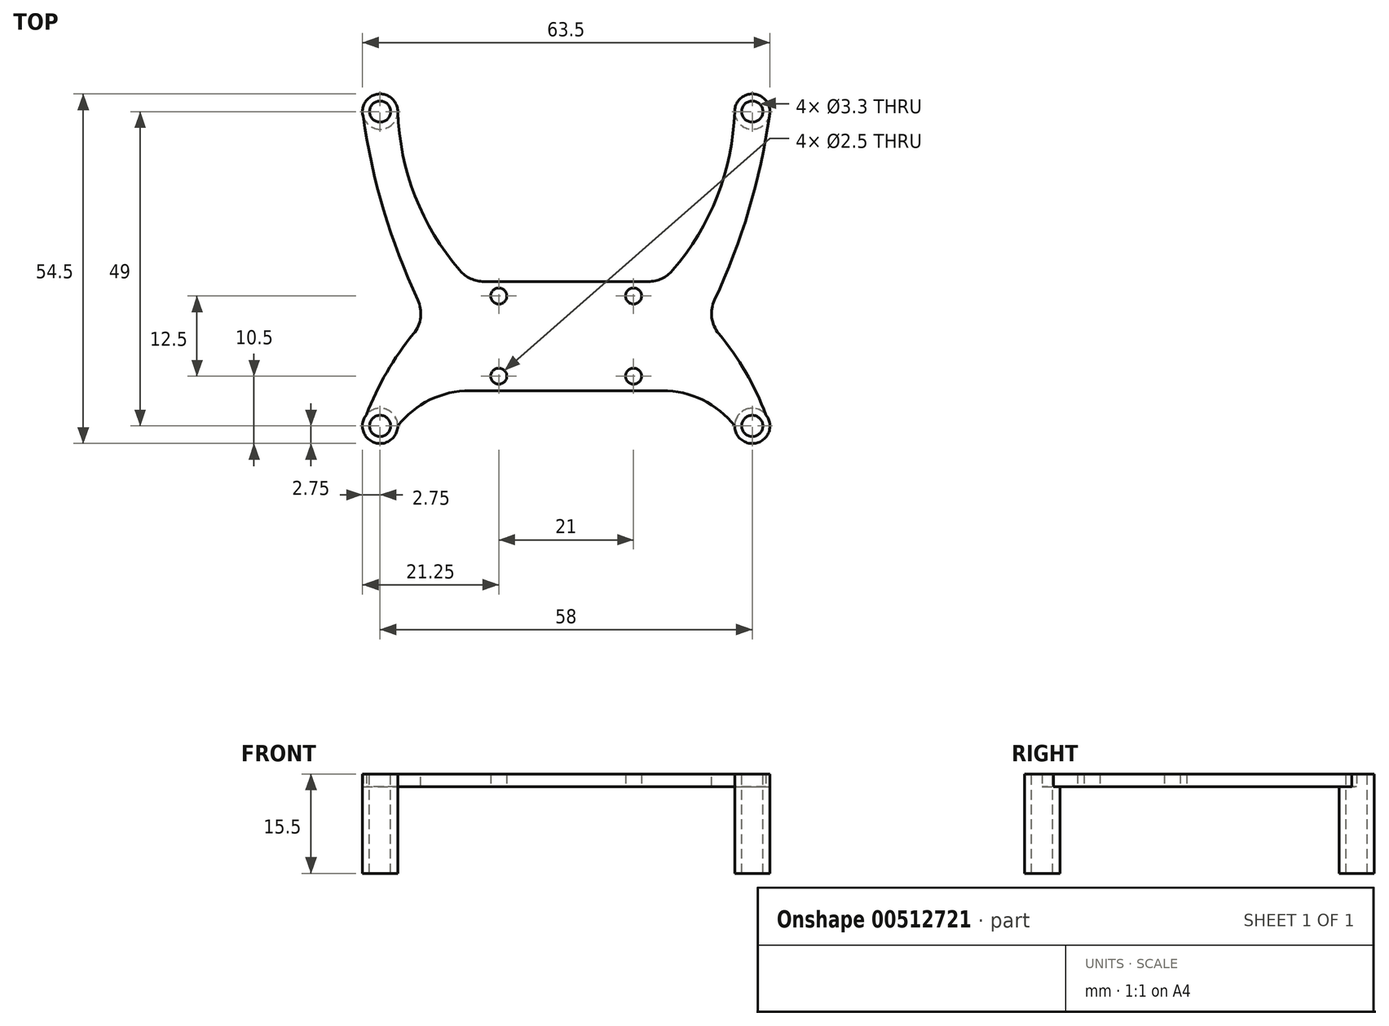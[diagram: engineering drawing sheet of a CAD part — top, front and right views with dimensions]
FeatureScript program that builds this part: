
annotation { "Feature Type Name" : "Feature", "Feature Type Description" : "" }
export const myFeature = defineFeature(function(context is Context, id is Id, definition is map)
    precondition{}
    {
        {
            var Q0;
            Q0=qCreatedBy(makeId("Top.planeOp"),FACE);
            var sketch = newSketch(context, id + "F0", { "sketchPlane" : qUnion([Q0])});
            skCircle(sketch, "E0", {"center": v(-29, 0) * mm, "radius": 2.75 * mm});
            skCircle(sketch, "E1", {"center": v(29, 0) * mm, "radius": 2.75 * mm});
            skLineSegment(sketch, "E2", {"start": v(-29, 0) * mm, "end": v(29, 0) * mm, "construction": true});
            skPoint(sketch, "E3", {"position": v(0, 0) * mm});
            skLineSegment(sketch, "E4.bottom", {"start": v(15, 22.5) * mm, "end": v(-15, 22.5) * mm});
            skLineSegment(sketch, "E4.top", {"start": v(15, 5.5) * mm, "end": v(-15, 5.5) * mm});
            skLineSegment(sketch, "E4.left", {"start": v(15, 22.5) * mm, "end": v(15, 5.5) * mm});
            skLineSegment(sketch, "E4.right", {"start": v(-15, 22.5) * mm, "end": v(-15, 5.5) * mm});
            skPoint(sketch, "E4.middle", {"position": v(0, 14) * mm});
            skPoint(sketch, "E5", {"position": v(-10.5, 20.25) * mm});
            skPoint(sketch, "E6", {"position": v(10.5, 20.25) * mm});
            skPoint(sketch, "E7", {"position": v(10.5, 7.75) * mm});
            skPoint(sketch, "E8", {"position": v(-10.5, 7.75) * mm});
            skLineSegment(sketch, "E9", {"start": v(-10.5, 20.25) * mm, "end": v(10.5, 7.75) * mm, "construction": true});
            skArc(sketch, "E10", {"start": v(-15, 22.5) * mm, "mid": v(-25.17, 12.59) * mm, "end": v(-31.75, 0) * mm});
            skArc(sketch, "E11", {"start": v(-15, 5.5) * mm, "mid": v(-21.26, 4.05) * mm, "end": v(-26.25, 0) * mm});
            skArc(sketch, "E12", {"start": v(26.25, 0) * mm, "mid": v(21.26, 4.05) * mm, "end": v(15, 5.5) * mm});
            skArc(sketch, "E13", {"start": v(31.75, 0) * mm, "mid": v(25.17, 12.59) * mm, "end": v(15, 22.5) * mm});
            skCircle(sketch, "E14", {"center": v(-29, 49) * mm, "radius": 2.75 * mm});
            skCircle(sketch, "E15", {"center": v(29, 49) * mm, "radius": 2.75 * mm});
            skArc(sketch, "E16", {"start": v(-26.25, 49) * mm, "mid": v(-23.1, 34.7) * mm, "end": v(-15, 22.5) * mm});
            skArc(sketch, "E17", {"start": v(15, 22.5) * mm, "mid": v(23.1, 34.7) * mm, "end": v(26.25, 49) * mm});
            skArc(sketch, "E18", {"start": v(15, 5.5) * mm, "mid": v(25.94, 26.26) * mm, "end": v(31.75, 49) * mm});
            skArc(sketch, "E19", {"start": v(-15, 5.5) * mm, "mid": v(-25.94, 26.26) * mm, "end": v(-31.75, 49) * mm});
            skSolve(sketch);
        }
        {
            var Q0;
            Q0 = qSketchRegion(id + "F0", true);
            extrude(context, id + "F1", {"entities" : qUnion([Q0]), "depth" : 2 * mm});
        }
        {
            var Q0;
            Q0=makeQuery(id+"F1.opExtrude","CAP_FACE",FACE,{"disambiguationData":[OSD([sQuery(id+"F0.wireOp",EDGE,"E0"),sQuery(id+"F0.wireOp",EDGE,"E1"),sQuery(id+"F0.wireOp",EDGE,"E4.bottom"),sQuery(id+"F0.wireOp",EDGE,"E4.top"),sQuery(id+"F0.wireOp",EDGE,"E10"),sQuery(id+"F0.wireOp",EDGE,"E11"),sQuery(id+"F0.wireOp",EDGE,"E12"),sQuery(id+"F0.wireOp",EDGE,"E13")])],"isStart":true});
            var sketch = newSketch(context, id + "F2", { "sketchPlane" : qUnion([Q0])});
            skCircle(sketch, "E20", {"center": v(29, 0) * mm, "radius": 2.75 * mm});
            skCircle(sketch, "E21", {"center": v(-29, 0) * mm, "radius": 2.75 * mm});
            skCircle(sketch, "E22", {"center": v(29, -49) * mm, "radius": 2.75 * mm});
            skCircle(sketch, "E23", {"center": v(-29, -49) * mm, "radius": 2.75 * mm});
            skSolve(sketch);
        }
        {
            var Q0;
            Q0 = qSketchRegion(id + "F2", true);
            extrude(context, id + "F3", {"entities" : qUnion([Q0]), "operationType" : NewBodyOperationType.ADD, "depth" : 13.5 * mm});
        }
        {
            var Q0;
            Q0=makeQuery(id+"F1.opExtrude","SWEPT_EDGE",EDGE,{"disambiguationData":[OSD([sQuery(id+"F0.wireOp",EDGE,"E4.bottom"),sQuery(id+"F0.wireOp",EDGE,"E4.left"),sQuery(id+"F0.wireOp",EDGE,"E13")])]});
            var Q1;
            Q1=makeQuery(id+"F1.opExtrude","SWEPT_EDGE",EDGE,{"disambiguationData":[OSD([sQuery(id+"F0.wireOp",EDGE,"E4.bottom"),sQuery(id+"F0.wireOp",EDGE,"E4.right"),sQuery(id+"F0.wireOp",EDGE,"E10")])]});
            var Q2;
            Q2=makeQuery(id+"F1.opExtrude","SWEPT_EDGE",EDGE,{"disambiguationData":[OSD([sQuery(id+"F0.wireOp",EDGE,"E10"),sQuery(id+"F0.wireOp",EDGE,"E19")])]});
            var Q3;
            Q3=makeQuery(id+"F1.opExtrude","SWEPT_EDGE",EDGE,{"disambiguationData":[OSD([sQuery(id+"F0.wireOp",EDGE,"E13"),sQuery(id+"F0.wireOp",EDGE,"E18")])]});
            fillet(context, id + "F4", {"entities" : qUnion([Q0, Q1, Q2, Q3]), "radius" : 5 * mm, "tangentPropagation" : true, "allowEdgeOverflow" : false});
        }
        {
            var Q0;
            Q0=sQuery(id+"F0.wireOp",VERTEX,"E2.end");
            var Q1;
            Q1=sQuery(id+"F0.wireOp",VERTEX,"E0.center");
            var Q2;
            Q2=sQuery(id+"F0.wireOp",VERTEX,"E14.center");
            var Q3;
            Q3=sQuery(id+"F0.wireOp",VERTEX,"E15.center");
            var Q4;
            Q4=makeQuery(id+"F1.opExtrude","SWEPT_BODY",BODY,{"disambiguationData":[OSD([sQuery(id+"F0.wireOp",EDGE,"E0"),sQuery(id+"F0.wireOp",EDGE,"E1"),sQuery(id+"F0.wireOp",EDGE,"E4.bottom"),sQuery(id+"F0.wireOp",EDGE,"E4.top"),sQuery(id+"F0.wireOp",EDGE,"E10"),sQuery(id+"F0.wireOp",EDGE,"E11"),sQuery(id+"F0.wireOp",EDGE,"E12"),sQuery(id+"F0.wireOp",EDGE,"E13")])]});
            hole(context, id + "F5", {"style" : HoleStyle.SIMPLE, "endStyle" : HoleEndStyle.THROUGH, "standardTappedOrClearance" : lookupTablePath({ "standard" : "ISO", "fit" : "Normal", "size" : "M3", "type" : "Clearance" }), "standardBlindInLast" : lookupTablePath({ "fit" : "Standard", "standard" : "ISO", "size" : "M3", "type" : "Clearance" }), "holeDiameter" : 3.3 * mm, "isTappedThrough" : true, "tappedDepth" : 12 * mm, "tapClearance" : 3, "locations" : qUnion([Q0, Q1, Q2, Q3]), "scope" : qUnion([Q4])});
        }
        {
            var Q0;
            Q0=sQuery(id+"F0.wireOp",VERTEX,"E0.center");
            var Q1;
            Q1=sQuery(id+"F0.wireOp",VERTEX,"E2.end");
            var Q2;
            Q2=sQuery(id+"F0.wireOp",VERTEX,"E14.center");
            var Q3;
            Q3=sQuery(id+"F0.wireOp",VERTEX,"E15.center");
            var Q4;
            Q4=makeQuery(id+"F1.opExtrude","SWEPT_BODY",BODY,{"disambiguationData":[OSD([sQuery(id+"F0.wireOp",EDGE,"E0"),sQuery(id+"F0.wireOp",EDGE,"E1"),sQuery(id+"F0.wireOp",EDGE,"E4.bottom"),sQuery(id+"F0.wireOp",EDGE,"E4.top"),sQuery(id+"F0.wireOp",EDGE,"E10"),sQuery(id+"F0.wireOp",EDGE,"E11"),sQuery(id+"F0.wireOp",EDGE,"E12"),sQuery(id+"F0.wireOp",EDGE,"E13")])]});
            hole(context, id + "F6", {"style" : HoleStyle.SIMPLE, "endStyle" : HoleEndStyle.THROUGH, "oppositeDirection" : true, "standardTappedOrClearance" : lookupTablePath({ "standard" : "ISO", "fit" : "Normal", "size" : "M3", "type" : "Clearance" }), "standardBlindInLast" : lookupTablePath({ "fit" : "Standard", "standard" : "ISO", "size" : "M3", "type" : "Clearance" }), "holeDiameter" : 3.3 * mm, "isTappedThrough" : true, "tappedDepth" : 12 * mm, "tapClearance" : 3, "locations" : qUnion([Q0, Q1, Q2, Q3]), "scope" : qUnion([Q4])});
        }
        {
            var Q0;
            Q0=sQuery(id+"F0.wireOp",VERTEX,"E8");
            var Q1;
            Q1=sQuery(id+"F0.wireOp",VERTEX,"E5");
            var Q2;
            Q2=sQuery(id+"F0.wireOp",VERTEX,"E6");
            var Q3;
            Q3=sQuery(id+"F0.wireOp",VERTEX,"E7");
            var Q4;
            Q4=makeQuery(id+"F1.opExtrude","SWEPT_BODY",BODY,{"disambiguationData":[OSD([sQuery(id+"F0.wireOp",EDGE,"E0"),sQuery(id+"F0.wireOp",EDGE,"E1"),sQuery(id+"F0.wireOp",EDGE,"E4.bottom"),sQuery(id+"F0.wireOp",EDGE,"E4.top"),sQuery(id+"F0.wireOp",EDGE,"E10"),sQuery(id+"F0.wireOp",EDGE,"E11"),sQuery(id+"F0.wireOp",EDGE,"E12"),sQuery(id+"F0.wireOp",EDGE,"E13")])]});
            hole(context, id + "F7", {"style" : HoleStyle.SIMPLE, "endStyle" : HoleEndStyle.THROUGH, "oppositeDirection" : true, "holeDiameter" : 2.5 * mm, "isTappedThrough" : true, "tappedDepth" : 12 * mm, "tapClearance" : 3, "locations" : qUnion([Q0, Q1, Q2, Q3]), "scope" : qUnion([Q4])});
        }
    });
